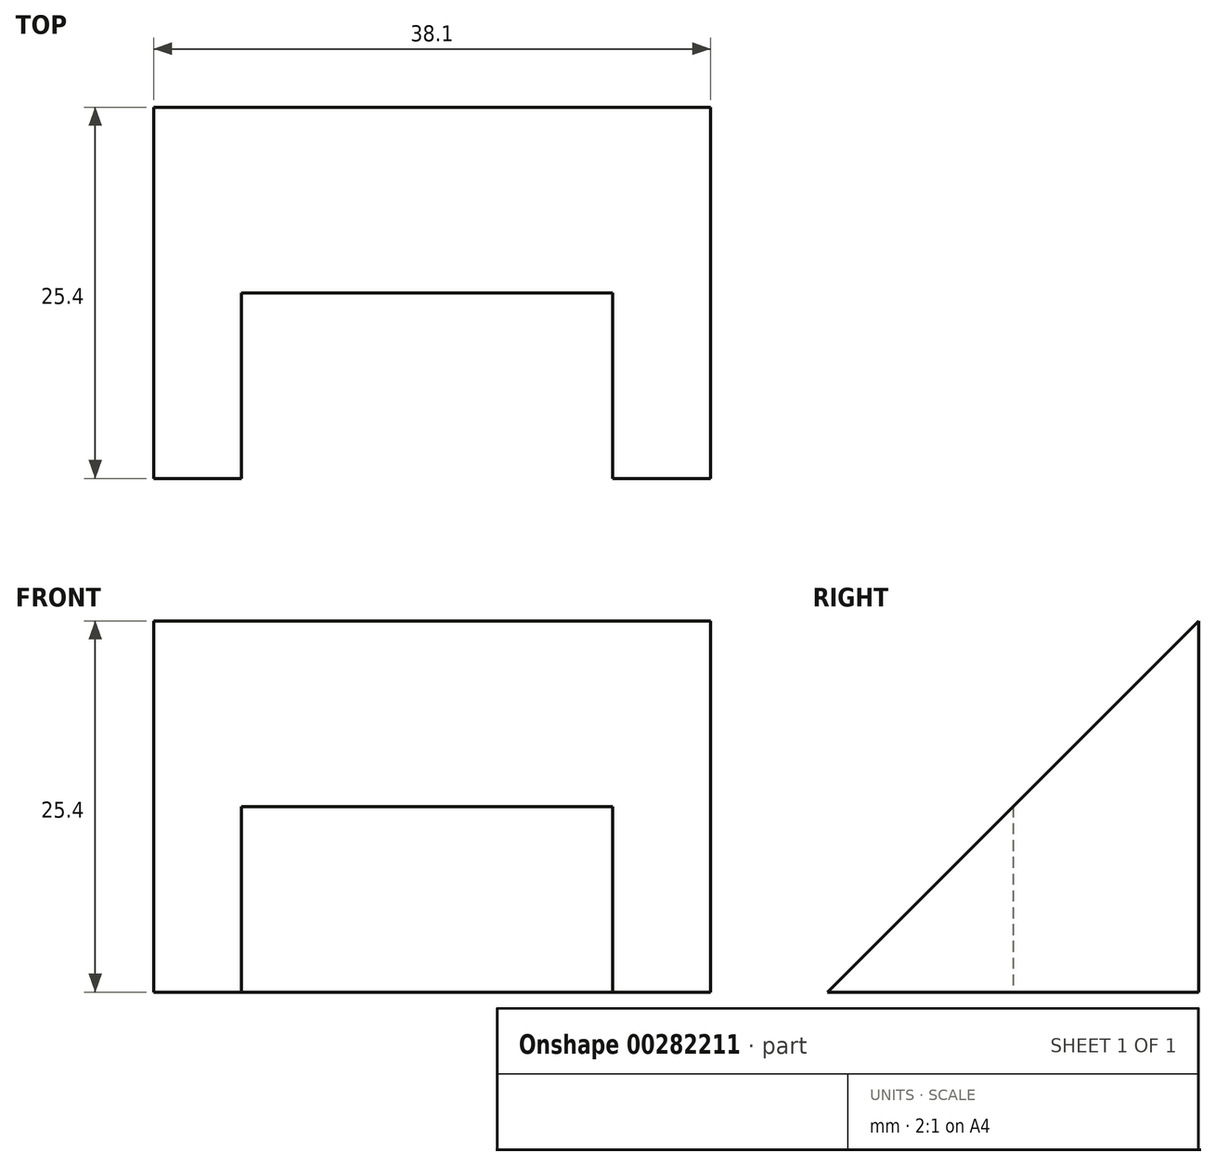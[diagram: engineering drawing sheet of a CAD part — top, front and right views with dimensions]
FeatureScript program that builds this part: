
annotation { "Feature Type Name" : "Feature", "Feature Type Description" : "" }
export const myFeature = defineFeature(function(context is Context, id is Id, definition is map)
    precondition{}
    {
        {
            var Q0;
            Q0=qCreatedBy(makeId("Right.planeOp"),FACE);
            var sketch = newSketch(context, id + "F0", { "sketchPlane" : qUnion([Q0])});
            skLineSegment(sketch, "E0", {"start": v(0, 25.4) * mm, "end": v(0, 0) * mm});
            skLineSegment(sketch, "E1", {"start": v(0, 0) * mm, "end": v(-25.4, 0) * mm});
            skLineSegment(sketch, "E2", {"start": v(-25.4, 0) * mm, "end": v(0, 25.4) * mm});
            skSolve(sketch);
        }
        {
            var Q0;
            Q0=makeQuery(id+"F0.imprint","IMPRINT",FACE,{"disambiguationData":[TD([[makeQuery(id+"F0.imprint","IMPRINT",EDGE,{"derivedFrom":sQuery(id+"F0.wireOp",EDGE,"E0")}),-1.0]])]});
            extrude(context, id + "F1", {"entities" : qUnion([Q0]), "endBound" : BoundingType.SYMMETRIC, "depth" : 38.1 * mm});
        }
        {
            var Q0;
            Q0=qCreatedBy(makeId("Top.planeOp"),FACE);
            var sketch = newSketch(context, id + "F2", { "sketchPlane" : qUnion([Q0])});
            skLineSegment(sketch, "E3", {"start": v(-13.04, -25.4) * mm, "end": v(-13.04, -12.7) * mm});
            skLineSegment(sketch, "E4", {"start": v(-13.04, -12.7) * mm, "end": v(12.36, -12.7) * mm});
            skLineSegment(sketch, "E5", {"start": v(12.36, -12.7) * mm, "end": v(12.36, -25.4) * mm});
            skLineSegment(sketch, "E6", {"start": v(12.36, -25.4) * mm, "end": v(-13.04, -25.4) * mm});
            skSolve(sketch);
        }
        {
            var Q0;
            Q0 = qSketchRegion(id + "F2", true);
            extrude(context, id + "F3", {"entities" : qUnion([Q0]), "operationType" : NewBodyOperationType.REMOVE, "depth" : 12.7 * mm});
        }
    });
